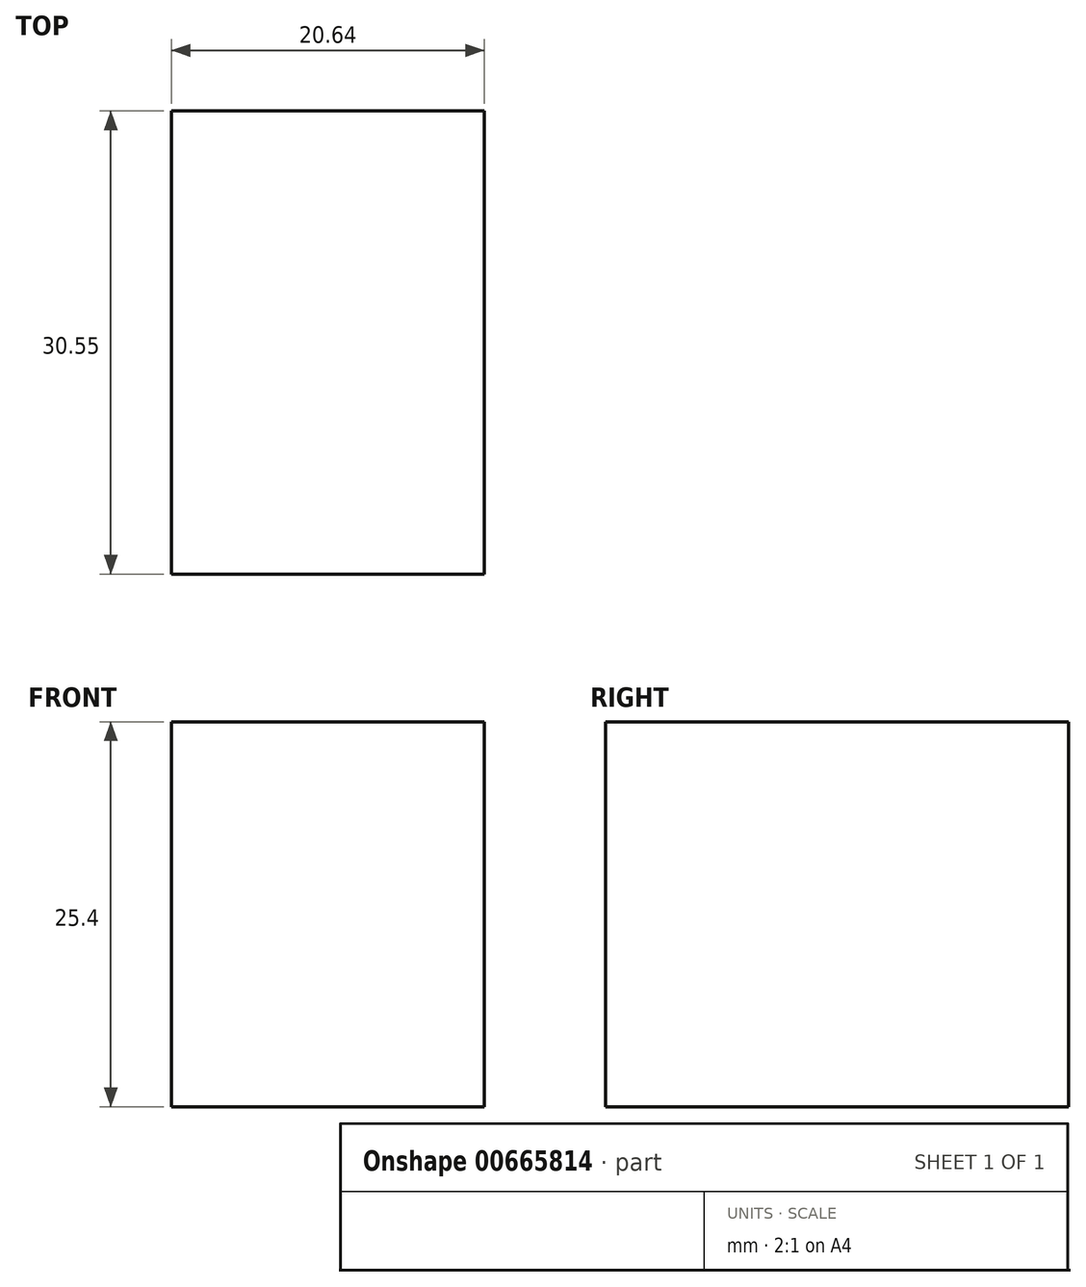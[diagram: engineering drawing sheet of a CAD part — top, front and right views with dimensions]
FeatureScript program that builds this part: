
annotation { "Feature Type Name" : "Feature", "Feature Type Description" : "" }
export const myFeature = defineFeature(function(context is Context, id is Id, definition is map)
    precondition{}
    {
        {
            var Q0;
            Q0=qCreatedBy(makeId("Top.planeOp"),FACE);
            var sketch = newSketch(context, id + "F0", { "sketchPlane" : qUnion([Q0])});
            skLineSegment(sketch, "E0.bottom", {"start": v(0, -8.54) * mm, "end": v(0, -8.54) * mm});
            skLineSegment(sketch, "E0.top", {"start": v(0, 0) * mm, "end": v(0, 0) * mm});
            skLineSegment(sketch, "E0.left", {"start": v(0, -8.54) * mm, "end": v(0, 0) * mm});
            skLineSegment(sketch, "E0.right", {"start": v(0, -8.54) * mm, "end": v(0, 0) * mm});
            skLineSegment(sketch, "E1.bottom", {"start": v(0, 9.83) * mm, "end": v(-20.64, 9.83) * mm});
            skLineSegment(sketch, "E1.top", {"start": v(0, 40.38) * mm, "end": v(-20.64, 40.38) * mm});
            skLineSegment(sketch, "E1.left", {"start": v(0, 9.83) * mm, "end": v(0, 40.38) * mm});
            skLineSegment(sketch, "E1.right", {"start": v(-20.64, 9.83) * mm, "end": v(-20.64, 40.38) * mm});
            skLineSegment(sketch, "E2.bottom", {"start": v(-9.89, -26.87) * mm, "end": v(-10.65, -26.87) * mm, "construction": true});
            skLineSegment(sketch, "E2.top", {"start": v(-9.89, -18.57) * mm, "end": v(-10.65, -18.57) * mm, "construction": true});
            skLineSegment(sketch, "E2.left", {"start": v(-9.89, -26.87) * mm, "end": v(-9.89, -18.57) * mm, "construction": true});
            skLineSegment(sketch, "E2.right", {"start": v(-10.65, -26.87) * mm, "end": v(-10.65, -18.57) * mm, "construction": true});
            skSolve(sketch);
        }
        {
            var Q0;
            Q0 = qSketchRegion(id + "F0", true);
            extrude(context, id + "F1", {"entities" : qUnion([Q0]), "depth" : 25.4 * mm, "offsetDistance" : 25.4 * mm});
        }
    });
